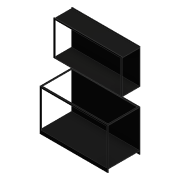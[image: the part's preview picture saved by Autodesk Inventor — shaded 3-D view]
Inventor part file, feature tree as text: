
AUTODESK INVENTOR PART (.ipt)
format: ipt  version: 2016 (Build 200138000, 138)  size: 251,392 bytes
history: native  units: mm
features: extrude x9, projected_geometry x9, sketch x8, plane x1
ambient origin geometry x8: Origin, YZ Plane, XZ Plane, XY Plane, X Axis, Y Axis, Z Axis, Center Point
bodies: Solid1 (feature_tree)
feature tree (27):
  extrude  "Extrusion1"  Depth=10.0mm
  extrude  "Extrusion2"  Depth=80.0mm
  extrude  "Extrusion3"  Depth=30.0mm
  extrude  "Extrusion4"  Depth=30.0mm
  plane  "Work Plane1"
  extrude  "Extrusion5"  Depth=10.0mm
  extrude  "Extrusion9"  Depth=10.0mm
  extrude  "Extrusión10"  Depth=30.0mm
  extrude  "Extrusión11"  TaperAngle=0.0deg  [1 undecoded]
  extrude  "Extrusion13"  Depth=2400.0mm
  sketch  "Sketch1"  dims[d3=0.0mm d5=10.0mm]
  sketch  "Sketch2"  dims[d6=10.0mm d7=80.0mm]
  projected_geometry  "Projected Loop1"
  sketch  "Sketch3"  dims[d9=0.0mm d10=30.0mm]
  projected_geometry  "Projected Loop2"
  sketch  "Sketch4"  dims[d11=400.0mm d12=0.0mm d13=30.0mm]
  projected_geometry  "Projected Loop3"
  projected_geometry  "Projected Loop4"
  projected_geometry  "Projected Loop5"
  sketch  "Sketch5"  dims[d14=30.0mm d15=10.0mm]
  sketch  "Sketch9"  dims[d16=0.0mm d18=10.0mm]
  projected_geometry  "Projected Loop9"
  sketch  "Boceto10"  dims[d19=0.0mm d32=30.0mm]
  projected_geometry  "Contorno proyectado10"
  projected_geometry  "Contorno proyectado11"
  sketch  "Sketch13"  dims[d33=10.0mm d34=0.0mm d36=2400.0mm d39=10.0mm d40=10.0mm d41=10.0mm d43=0.0mm d44=30.0mm d45=30.0mm d46=30.0mm d48=750.0mm d49=0.0mm d53=10.0mm d54=20.0mm d55=2400.0mm d56=0.0mm]
  projected_geometry  "Projected Loop12"
note: 1 required parameter value undecoded (feature->parameter linkage not recoverable at this tier; creation-order binding heuristic only, values carry confidence <= 0.55)
